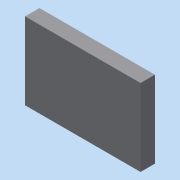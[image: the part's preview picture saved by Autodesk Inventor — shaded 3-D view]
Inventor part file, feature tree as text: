
AUTODESK INVENTOR PART (.ipt)
format: ipt  version: 2016 (Build 200138000, 138)  size: 68,096 bytes
history: native  units: in
note: dims shown in document units (in); Inventor stores cm internally (conversion verified against a paired STEP export)
features: extrude x1, sketch x1
ambient origin geometry x8: Origin, YZ Plane, XZ Plane, XY Plane, X Axis, Y Axis, Z Axis, Center Point
bodies: Solid1 (feature_tree)
feature tree (2):
  extrude  "Extrusion1"  Depth=1.5in
  sketch  "Sketch1"  dims[d0=1.0in d1=1.5in d2=0.187in d3=0.0in]
